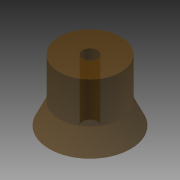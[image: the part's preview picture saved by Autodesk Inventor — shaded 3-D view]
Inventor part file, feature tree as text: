
AUTODESK INVENTOR PART (.ipt)
format: ipt  version: 2014 (Build 180170000, 170)  size: 90,624 bytes
history: native  units: in
note: dims shown in document units (in); Inventor stores cm internally (conversion verified against a paired STEP export)
features: sketch x2, revolve x1, extrude x1
ambient origin geometry x8: Origin, YZ Plane, XZ Plane, XY Plane, X Axis, Y Axis, Z Axis, Center Point
bodies: Solid1 (feature_tree)
feature tree (4):
  revolve  "Revolution1"  [1 undecoded]
  extrude  "Extrusion1"  Depth=0.25in
  sketch  "Sketch1"  dims[d0=0.33in d1=0.5in]
  sketch  "Sketch2"  dims[d2=0.33in d3=0.25in d4=90.0deg d5=0.12in d6=1.0in d7=0.0in]
note: 1 required parameter value undecoded (feature->parameter linkage not recoverable at this tier; creation-order binding heuristic only, values carry confidence <= 0.55)
